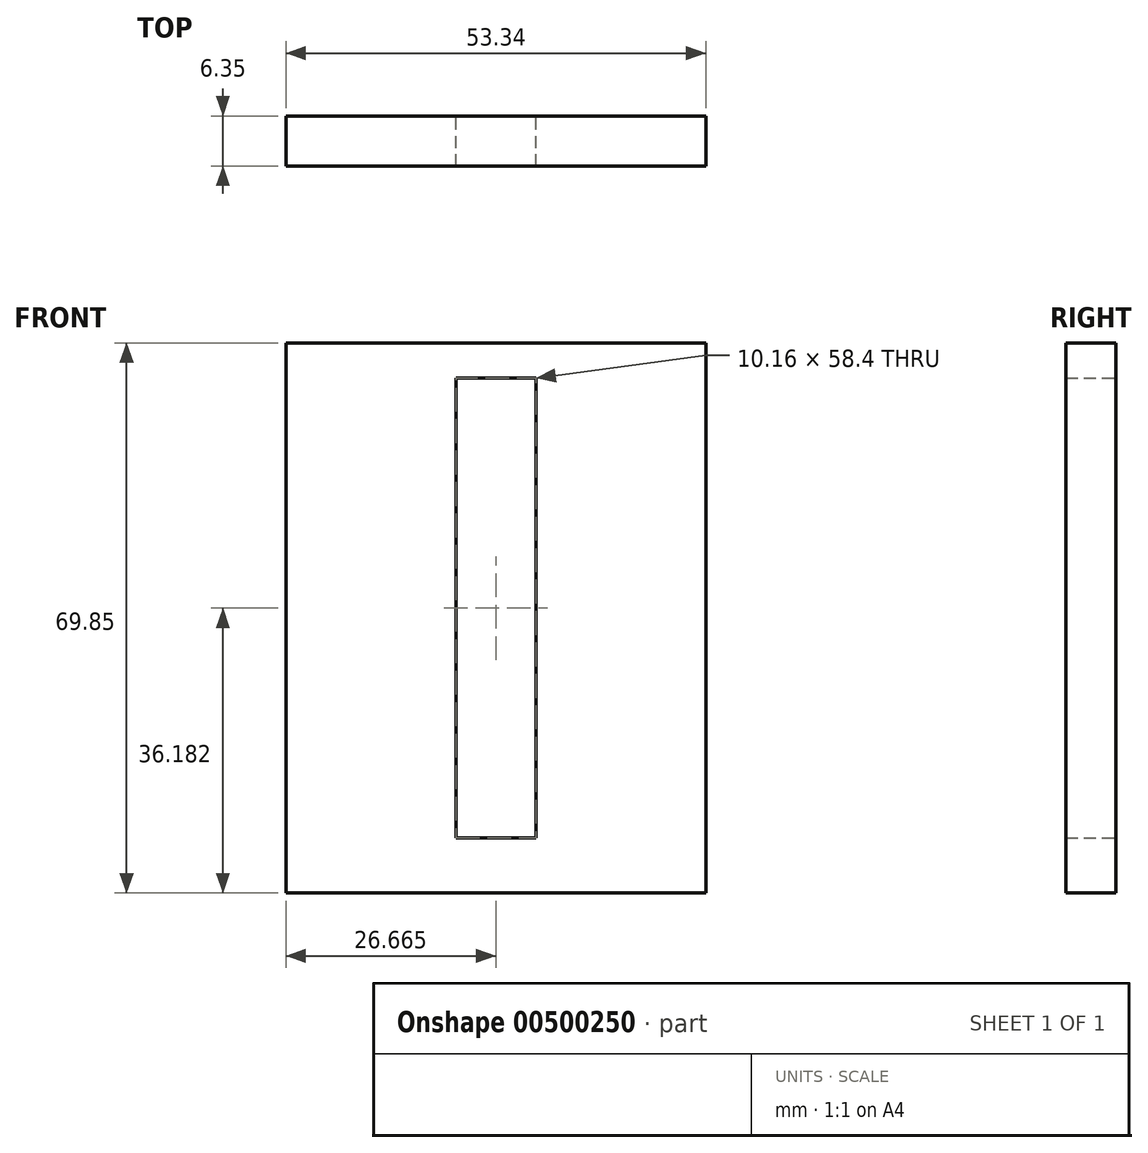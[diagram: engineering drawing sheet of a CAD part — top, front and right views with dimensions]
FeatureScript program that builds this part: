
annotation { "Feature Type Name" : "Feature", "Feature Type Description" : "" }
export const myFeature = defineFeature(function(context is Context, id is Id, definition is map)
    precondition{}
    {
        {
            var Q0;
            Q0=qCreatedBy(makeId("Front.planeOp"),FACE);
            var sketch = newSketch(context, id + "F0", { "sketchPlane" : qUnion([Q0])});
            skLineSegment(sketch, "E0.bottom", {"start": v(-7.75, 40.46) * mm, "end": v(45.59, 40.46) * mm});
            skLineSegment(sketch, "E0.top", {"start": v(-7.75, -29.4) * mm, "end": v(45.59, -29.4) * mm});
            skLineSegment(sketch, "E0.left", {"start": v(-7.75, 40.46) * mm, "end": v(-7.75, -29.4) * mm});
            skLineSegment(sketch, "E0.right", {"start": v(45.59, 40.46) * mm, "end": v(45.59, -29.4) * mm});
            skLineSegment(sketch, "E1", {"start": v(24, 5.53) * mm, "end": v(24, -12.25) * mm});
            skLineSegment(sketch, "E2", {"start": v(24, -12.25) * mm, "end": v(24, 25.83) * mm});
            skLineSegment(sketch, "E3", {"start": v(13.84, 5.53) * mm, "end": v(13.84, 23.31) * mm});
            skLineSegment(sketch, "E4", {"start": v(13.84, 23.31) * mm, "end": v(13.84, 25.83) * mm});
            skLineSegment(sketch, "E5", {"start": v(13.84, 5.53) * mm, "end": v(13.84, -12.25) * mm});
            skLineSegment(sketch, "E6", {"start": v(13.84, -12.25) * mm, "end": v(13.84, -22.4) * mm});
            skLineSegment(sketch, "E7", {"start": v(13.84, -22.4) * mm, "end": v(24, -22.4) * mm});
            skLineSegment(sketch, "E8", {"start": v(24, -22.4) * mm, "end": v(24, -12.25) * mm});
            skLineSegment(sketch, "E9", {"start": v(24, 25.83) * mm, "end": v(24, 36) * mm});
            skLineSegment(sketch, "E10", {"start": v(24, 36) * mm, "end": v(13.84, 36) * mm});
            skLineSegment(sketch, "E11", {"start": v(13.84, 36) * mm, "end": v(13.84, 25.83) * mm});
            skPoint(sketch, "E12.start.orphan", {"position": v(18.92, 5.53) * mm});
            skPoint(sketch, "E13.trimOffspring.end.orphan", {"position": v(18.92, -29.4) * mm});
            skPoint(sketch, "E14.start.orphan", {"position": v(18.92, 40.46) * mm});
            skSolve(sketch);
        }
        {
            var Q0;
            Q0 = qSketchRegion(id + "F0", true);
            extrude(context, id + "F1", {"entities" : qUnion([Q0]), "depth" : 6.35 * mm});
        }
    });
